# Revit family: lpb-350_500kx5-k_50Hz
name_source: partatom
category: 機械設備
units: mm (PartAtom-declared; Revit-internal decimal feet)

## family parameters
OmniClass タイトル = Heat Exchangers for Ventilation Air
OmniClass 番号 = 23.75.10.34.21
パーツ タイプ = 標準
ロード時にボイドで切り取り = いいえ
丸型コネクタ寸法 = 直径を使用
作業面ベース = いいえ
共有 = いいえ
常に垂直 = はい
部屋計算ポイント = いいえ

## types (2) — shared parameters
Clearance Front = 600
Duct_D = 30
Duct_EA_W = 6  [stored 0.019685 ft]
Duct_Height = 50  [stored 0.164042 ft]
Duct_SA_W = 6  [stored 0.019685 ft]
EAサイズ_W = 280  [stored 0.918635 ft]
H1 = 700
IfcExportAs = IfcAirToAirHeatRecoveryType
IfcExportType = ROTARYWHEEL
MID静圧 = 0.0 Pa
MID風量 = 0.0 m³/h
MIN静圧 = 0.0 Pa
MIN風量 = 0.0 m³/h
OAサイズ_W = 280  [stored 0.918635 ft]
OmniClassCode = 23-27 23 19 11
RAサイズ_W = 280  [stored 0.918635 ft]
SAサイズ_W = 280  [stored 0.918635 ft]
URL = https://www.mitsubishielectric.co.jp
Uniclass2015Code = Pr_60_60_36_88
Uniclass2015Title = Thermal wheels
Uniclass2015Version = Systems v1.9
W2 = 555  [stored 1.82087 ft]
エンタルピ交換効率_冷房 = 60.50%
エンタルピ交換効率_暖房 = 66.50%
ドレン管_H = 65  [stored 0.213255 ft]
ドレン管_Width = 46  [stored 0.150919 ft]
ドレン管径 = 27 mm
メンテナンススペース = はい
仕様書バージョン = Version1.0
企業コード = 108420
分類コード = 50052504100050
初期抵抗 = 0.0 Pa
加湿給水管径 = 22 mm
参照している仕様書等のバージョン = 公共建築工事標準仕様書（機械設備工事編）平成31年度版
周波数 = 50 Hz
呼称 = 全熱交換ユニット
外気量 = 0.0 m³/h
実風量 = 0.0 m³/h
形式 = 床置形
排気量 = 0.0 m³/h
本体マテリアル = 溶融亜鉛めっき鋼板
本体固定用穴_径 = 20  [stored 0.0656168 ft]
極数 = 3
法定耐用年数 = 15
温度交換効率 = 77.00%
相 = 3
積算_科目 = 1 空気調和設備
符号 = HEU
給水管_D = 131  [stored 0.42979 ft]
給水管_H = 316
給水管_Width = 46  [stored 0.150919 ft]
製品リリース年月 = 2018/7/25
製品出荷対象 = 国内
製造元 = 三菱電機株式会社
設置方法 = 床置形
設計風量 = 0.0 m³/h
説明 = 設備用ロスナイ 床置ビルトイン形機械室設置タイプ加湿付
負荷分類 = 3_ファン類
運転質量 = 0.00 kg
電圧 = 200 V
zero-valued in all types: Clearance Back, Clearance Bottom, Clearance Left, Clearance Right, Clearance Top

## per-type parameters (varying)
- LPB-350KX5-K: D1=1500  [stored 4.92126 ft]; D2=1007  [stored 3.30381 ft]; D3=188; Depth=1328  [stored 4.35696 ft]; Duct_OA_W=475  [stored 1.5584 ft]; Duct_RA_W=150; EAサイズ_D=540  [stored 1.77165 ft]; H2=1750; Height=1486  [stored 4.87533 ft]; MAX静圧=196.0 Pa; MAX風量=3500.0 m³/h; OAサイズ_D=540  [stored 1.77165 ft]; RAサイズ_D=540  [stored 1.77165 ft]; SAサイズ_D=540  [stored 1.77165 ft]; W1=1200; Width=1200; ドレン管_D=326  [stored 1.06955 ft]; 価格=8395000 $; 有効加湿量=8.8; 本体固定用穴ピッチ1=1710  [stored 5.61024 ft]; 本体固定用穴ピッチ2=650  [stored 2.13255 ft]; 本体固定用穴ピッチ3=300; 機外静圧=196.0 Pa; 機外静圧_排気=196.0 Pa; 消費電力=2550 W; 製品質量=584.00 kg; 質量=700.80 kg; 電動機出力=2 W; 面風速=6.4 m/s; 風量=3500.0 m³/h; 騒音レベル(dB(A))=51
- LPB-500KX5-K: D1=1690  [stored 5.54462 ft]; D2=1240  [stored 4.06824 ft]; D3=190; Depth=1690  [stored 5.54462 ft]; Duct_OA_W=528  [stored 1.73228 ft]; Duct_RA_W=202  [stored 0.66273 ft]; EAサイズ_D=720  [stored 2.3622 ft]; H2=2000  [stored 6.56168 ft]; Height=1586  [stored 5.20341 ft]; MAX静圧=250.0 Pa; MAX風量=5000.0 m³/h; OAサイズ_D=720  [stored 2.3622 ft]; RAサイズ_D=720  [stored 2.3622 ft]; SAサイズ_D=720  [stored 2.3622 ft]; W1=1300  [stored 4.26509 ft]; Width=1300  [stored 4.26509 ft]; ドレン管_D=256  [stored 0.839895 ft]; 価格=10442000 $; 有効加湿量=12.5; 本体固定用穴ピッチ1=1810  [stored 5.93832 ft]; 本体固定用穴ピッチ2=750  [stored 2.46063 ft]; 本体固定用穴ピッチ3=450  [stored 1.47638 ft]; 機外静圧=250.0 Pa; 機外静圧_排気=250.0 Pa; 消費電力=4250 W; 製品質量=737.00 kg; 質量=884.40 kg; 電動機出力=4 W; 面風速=6.9 m/s; 風量=5000.0 m³/h; 騒音レベル(dB(A))=55

note: column(s) folded — value = type name in every type: モデル

note: [stored X ft] marks values corroborated as IEEE doubles in the binary element streams (Revit-internal decimal feet)

## geometry (parser evidence)
native form markers: Blend x2
no freeform markers — native parametric forms only
